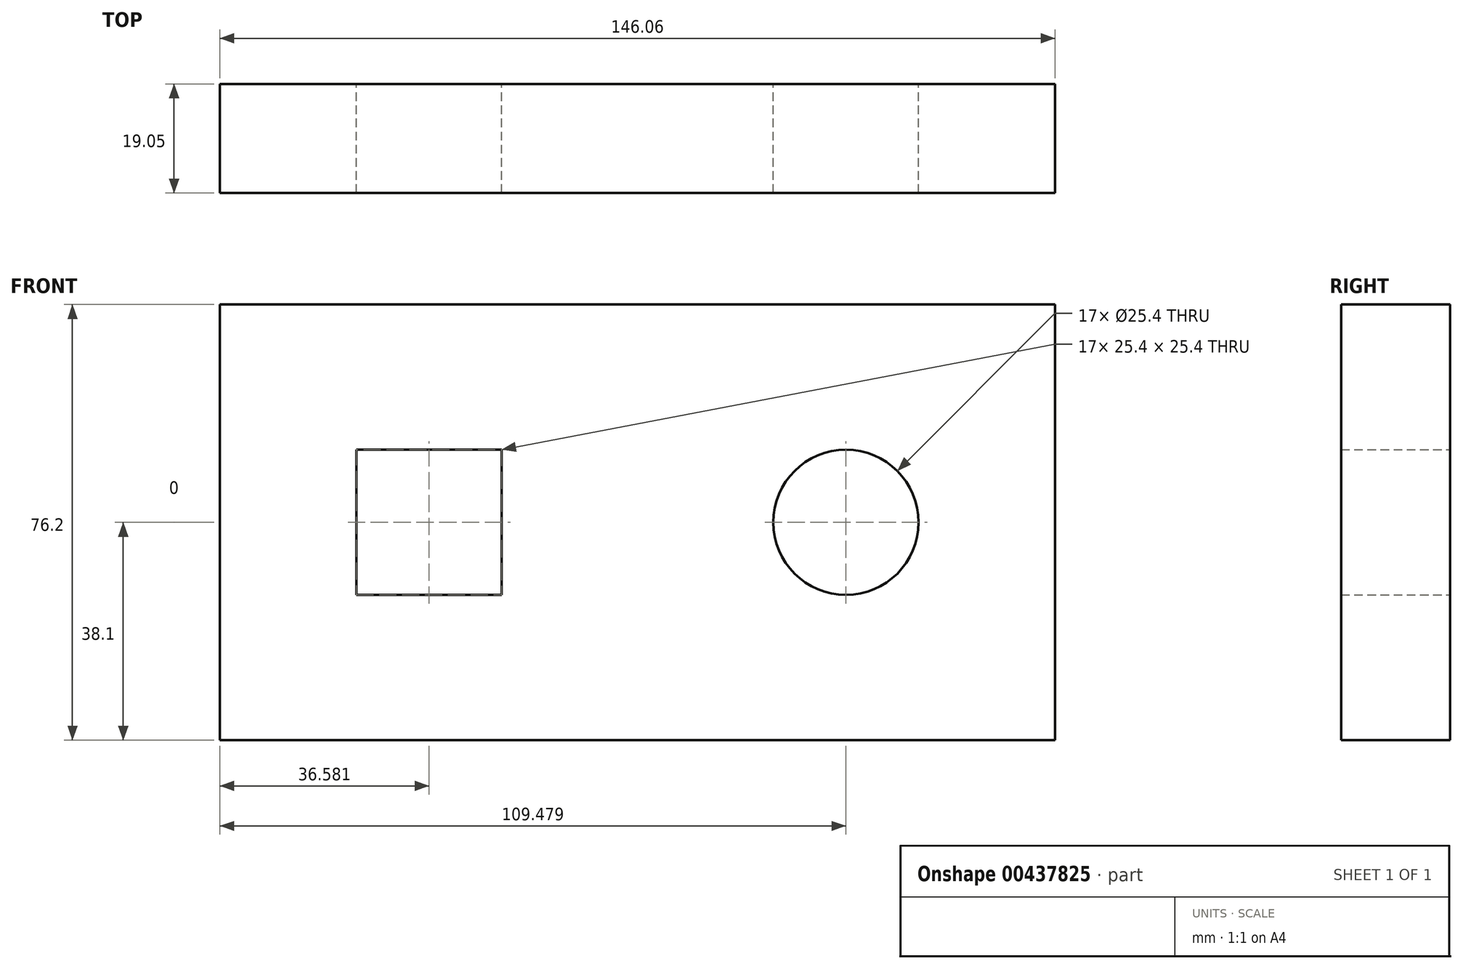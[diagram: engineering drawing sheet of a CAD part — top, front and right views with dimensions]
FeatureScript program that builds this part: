
annotation { "Feature Type Name" : "Feature", "Feature Type Description" : "" }
export const myFeature = defineFeature(function(context is Context, id is Id, definition is map)
    precondition{}
    {
        {
            var Q0;
            Q0=qCreatedBy(makeId("Front.planeOp"),FACE);
            var sketch = newSketch(context, id + "F0", { "sketchPlane" : qUnion([Q0])});
            skLineSegment(sketch, "E0.bottom", {"start": v(73.03, 38.1) * mm, "end": v(-73.03, 38.1) * mm});
            skLineSegment(sketch, "E0.top", {"start": v(73.03, -38.1) * mm, "end": v(-73.03, -38.1) * mm});
            skLineSegment(sketch, "E0.left", {"start": v(73.03, 38.1) * mm, "end": v(73.03, -38.1) * mm});
            skLineSegment(sketch, "E0.right", {"start": v(-73.03, 38.1) * mm, "end": v(-73.03, -38.1) * mm});
            skPoint(sketch, "E0.middle", {"position": v(0, 0) * mm});
            skLineSegment(sketch, "E1.bottom", {"start": v(-23.75, 12.7) * mm, "end": v(-49.15, 12.7) * mm});
            skLineSegment(sketch, "E1.top", {"start": v(-23.75, -12.7) * mm, "end": v(-49.15, -12.7) * mm});
            skLineSegment(sketch, "E1.left", {"start": v(-23.75, 12.7) * mm, "end": v(-23.75, -12.7) * mm});
            skLineSegment(sketch, "E1.right", {"start": v(-49.15, 12.7) * mm, "end": v(-49.15, -12.7) * mm});
            skPoint(sketch, "E1.middle", {"position": v(-36.45, 0) * mm});
            skCircle(sketch, "E2", {"center": v(36.45, 0) * mm, "radius": 12.7 * mm});
            skSolve(sketch);
        }
        {
            var Q0;
            Q0=makeQuery(id+"F0.imprint","IMPRINT",FACE,{"disambiguationData":[TD([[makeQuery(id+"F0.imprint","IMPRINT",EDGE,{"derivedFrom":sQuery(id+"F0.wireOp",EDGE,"E0.bottom")}),1.0]])]});
            extrude(context, id + "F1", {"entities" : qUnion([Q0]), "depth" : 19.05 * mm});
        }
    });
